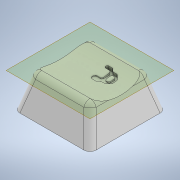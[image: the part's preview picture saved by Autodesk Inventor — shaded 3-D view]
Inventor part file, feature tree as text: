
AUTODESK INVENTOR PART (.ipt)
format: ipt  version: 2022 (Build 260153000, 153)  size: 294,400 bytes
history: native  units: in
note: dims shown in document units (in); Inventor stores cm internally (conversion verified against a paired STEP export)
features: extrude x6, sketch x6, plane x2, fillet x1
ambient origin geometry x8: Origin, YZ Plane, XZ Plane, XY Plane, X Axis, Y Axis, Z Axis, Center Point
bodies: Solid1 (feature_tree)
feature tree (15):
  extrude  "Extrusion1"  Depth=0.7087in
  fillet  "Fillet1"  Radius=0.315in
  plane  "Work Plane1"
  extrude  "Extrusion2"  Depth=0.4724in
  extrude  "Extrusion3"  Depth=0.6299in
  extrude  "Extrusion4"  Depth=0.1772in
  extrude  "Extrusion5"  Depth=0.1575in TaperAngle=0.0deg
  plane  "Work Plane2"
  extrude  "Extrusion6"  Depth=0.1634in
  sketch  "Sketch1"  dims[d0=0.7087in d1=0.7087in d2=0.315in d3=-0.1031in]
  sketch  "Sketch2"  dims[d4=0.0591in d5=0.4724in]
  sketch  "Sketch3"  dims[d6=0.0in d7=0.0in d8=0.6299in]
  sketch  "Sketch4"  dims[d9=0.6299in d10=0.1772in d11=-0.1031in]
  sketch  "Sketch5"  dims[d12=0.2185in d13=0.1575in d14=0.0in]
  sketch  "Sketch6"  dims[d15=0.0472in d16=0.1634in d17=0.1634in d18=0.0472in d19=0.0118in d20=0.1575in d21=0.0in d22=0.063in d23=0.0in]
